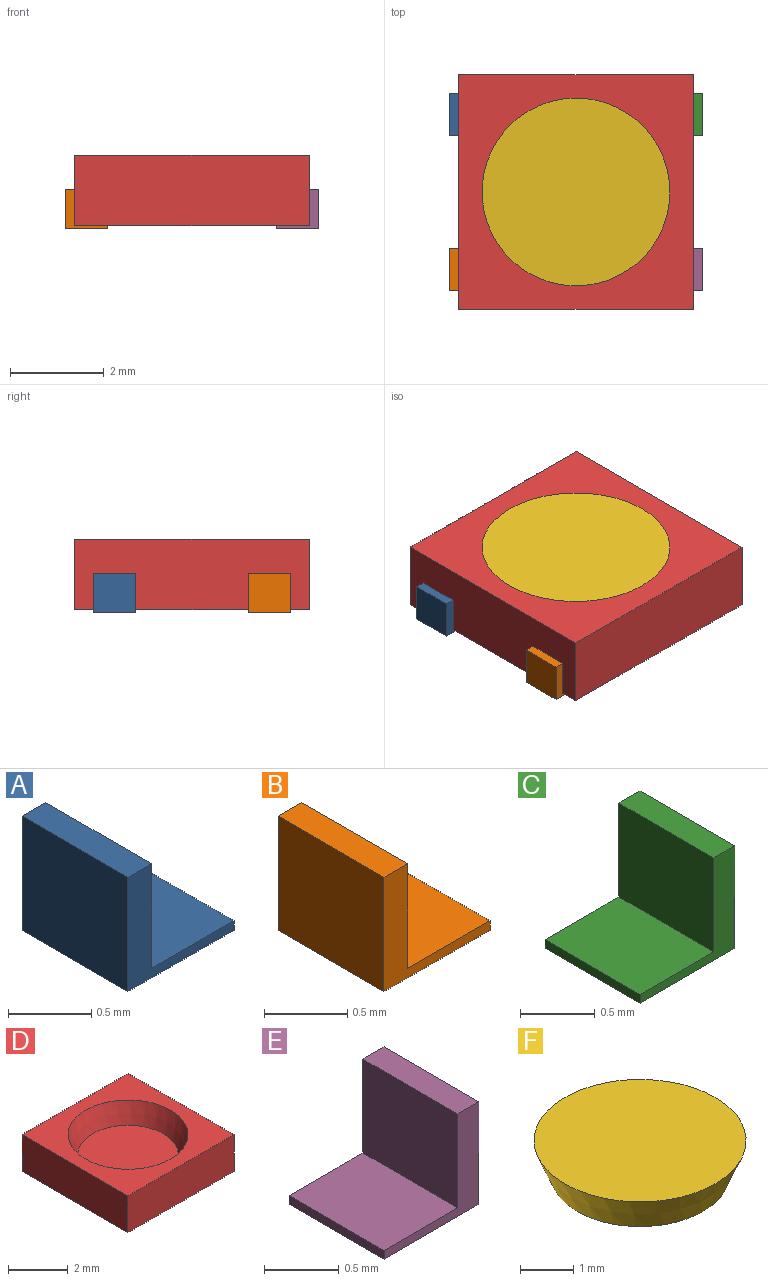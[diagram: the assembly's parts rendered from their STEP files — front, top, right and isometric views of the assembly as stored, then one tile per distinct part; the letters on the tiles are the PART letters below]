
ASSEMBLY  parts=6 mates=5
PART A: 8 faces, bbox 0.9x0.9x0.8 mm
  f0: plane 0.9x0.7mm, normal (0,0,1), area 0.6mm2, adj f1,f2,f3,f6
  f1: plane 0.9x0.84mm, normal (0,1,0), area 0.2mm2, adj f0,f2,f4,f5,f6,f7
  f2: plane 0.9x0.07mm, normal (1,0,0), area 0.1mm2, adj f0,f1,f3,f5
  f3: plane 0.9x0.84mm, normal (0,-1,0), area 0.2mm2, adj f0,f2,f4,f5,f6,f7
  f4: plane 0.9x0.84mm, normal (-1,0,0), area 0.8mm2, adj f1,f3,f5,f7
  f5: plane 0.9x0.9mm, normal (0,0,-1), area 0.8mm2, adj f1,f2,f3,f4
  f6: plane 0.9x0.77mm, normal (1,0,0), area 0.7mm2, adj f0,f1,f3,f7
  f7: plane 0.9x0.2mm, normal (0,0,1), area 0.2mm2, adj f1,f3,f4,f6
PART B: 8 faces, bbox 0.9x0.9x0.8 mm
  f0: plane 0.9x0.7mm, normal (0,0,1), area 0.6mm2, adj f1,f2,f3,f6
  f1: plane 0.9x0.84mm, normal (0,1,0), area 0.2mm2, adj f0,f2,f4,f5,f6,f7
  f2: plane 0.9x0.07mm, normal (1,0,0), area 0.1mm2, adj f0,f1,f3,f5
  f3: plane 0.9x0.84mm, normal (0,-1,0), area 0.2mm2, adj f0,f2,f4,f5,f6,f7
  f4: plane 0.9x0.84mm, normal (-1,0,0), area 0.8mm2, adj f1,f3,f5,f7
  f5: plane 0.9x0.9mm, normal (0,0,-1), area 0.8mm2, adj f1,f2,f3,f4
  f6: plane 0.9x0.77mm, normal (1,0,0), area 0.7mm2, adj f0,f1,f3,f7
  f7: plane 0.9x0.2mm, normal (0,0,1), area 0.2mm2, adj f1,f3,f4,f6
PART C: 8 faces, bbox 0.9x0.9x0.8 mm
  f0: plane 0.9x0.84mm, normal (0,1,0), area 0.2mm2, adj f1,f3,f4,f5,f6,f7
  f1: plane 0.9x0.84mm, normal (1,0,0), area 0.8mm2, adj f0,f2,f4,f7
  f2: plane 0.9x0.84mm, normal (0,-1,0), area 0.2mm2, adj f1,f3,f4,f5,f6,f7
  f3: plane 0.9x0.07mm, normal (-1,0,0), area 0.1mm2, adj f0,f2,f4,f5
  f4: plane 0.9x0.9mm, normal (0,0,-1), area 0.8mm2, adj f0,f1,f2,f3
  f5: plane 0.9x0.7mm, normal (0,0,1), area 0.6mm2, adj f0,f2,f3,f6
  f6: plane 0.9x0.77mm, normal (-1,0,0), area 0.7mm2, adj f0,f2,f5,f7
  f7: plane 0.9x0.2mm, normal (0,0,1), area 0.2mm2, adj f0,f1,f2,f6
PART D: 8 faces, bbox 5x5x1.5 mm
  f0: plane 5x1.5mm, normal (0,-1,0), area 7.5mm2, adj f1,f3,f4,f7
  f1: plane 5x1.5mm, normal (1,0,0), area 7.5mm2, adj f0,f2,f4,f7
  f2: plane 5x1.5mm, normal (0,1,0), area 7.5mm2, adj f1,f3,f4,f7
  f3: plane 5x1.5mm, normal (-1,0,0), area 7.5mm2, adj f0,f2,f4,f7
  f4: plane 5x5mm, normal (0,0,1), area 12.4mm2, adj f0,f1,f2,f3,f5
  f5: cone r=1.68mm half-angle=22.1deg, axis (0,0,1), area 10mm2, adj f4,f6
  f6: plane 3.35x3.35mm, normal (0,0,1), area 8.8mm2, adj f5
  f7: plane 5x5mm, normal (0,0,-1), area 25mm2, adj f0,f1,f2,f3
PART E: 8 faces, bbox 0.9x0.9x0.8 mm
  f0: plane 0.9x0.84mm, normal (0,1,0), area 0.2mm2, adj f1,f3,f4,f5,f6,f7
  f1: plane 0.9x0.84mm, normal (1,0,0), area 0.8mm2, adj f0,f2,f4,f7
  f2: plane 0.9x0.84mm, normal (0,-1,0), area 0.2mm2, adj f1,f3,f4,f5,f6,f7
  f3: plane 0.9x0.07mm, normal (-1,0,0), area 0.1mm2, adj f0,f2,f4,f5
  f4: plane 0.9x0.9mm, normal (0,0,-1), area 0.8mm2, adj f0,f1,f2,f3
  f5: plane 0.9x0.7mm, normal (0,0,1), area 0.6mm2, adj f0,f2,f3,f6
  f6: plane 0.9x0.77mm, normal (-1,0,0), area 0.7mm2, adj f0,f2,f5,f7
  f7: plane 0.9x0.2mm, normal (0,0,1), area 0.2mm2, adj f0,f1,f2,f6
PART F: 3 faces, bbox 4x4x0.8 mm
  f0: plane 3.35x3.35mm, normal (0,0,-1), area 8.8mm2, adj f2
  f1: plane 4x4mm, normal (0,0,1), area 12.6mm2, adj f2
  f2: cone r=1.68mm half-angle=22.1deg, axis (0,0,1), area 10mm2, adj f0,f1
PLACE A t=(0,0,0.78)mm
PLACE B t=(0,0,0.78)mm
PLACE C t=(0,0,0.78)mm
PLACE D t=(0,0,0.78)mm
PLACE E t=(0,0,0.78)mm
PLACE F t=(0,0,0.78)mm
MATE fastened F.f2 <-> D.f5  axis (0,0,-1) through (0,0,-0.02)mm
MATE fastened C.f5 <-> D.f7  axis (0,0,1) through (2.5,2.1,-0.72)mm
MATE fastened A.f0 <-> D.f7  axis (0,0,1) through (-2.5,2.1,-0.72)mm
MATE fastened E.f5 <-> D.f7  axis (0,0,1) through (2.5,-2.1,-0.72)mm
MATE fastened B.f0 <-> D.f7  axis (0,0,1) through (-2.5,-2.1,-0.72)mm
